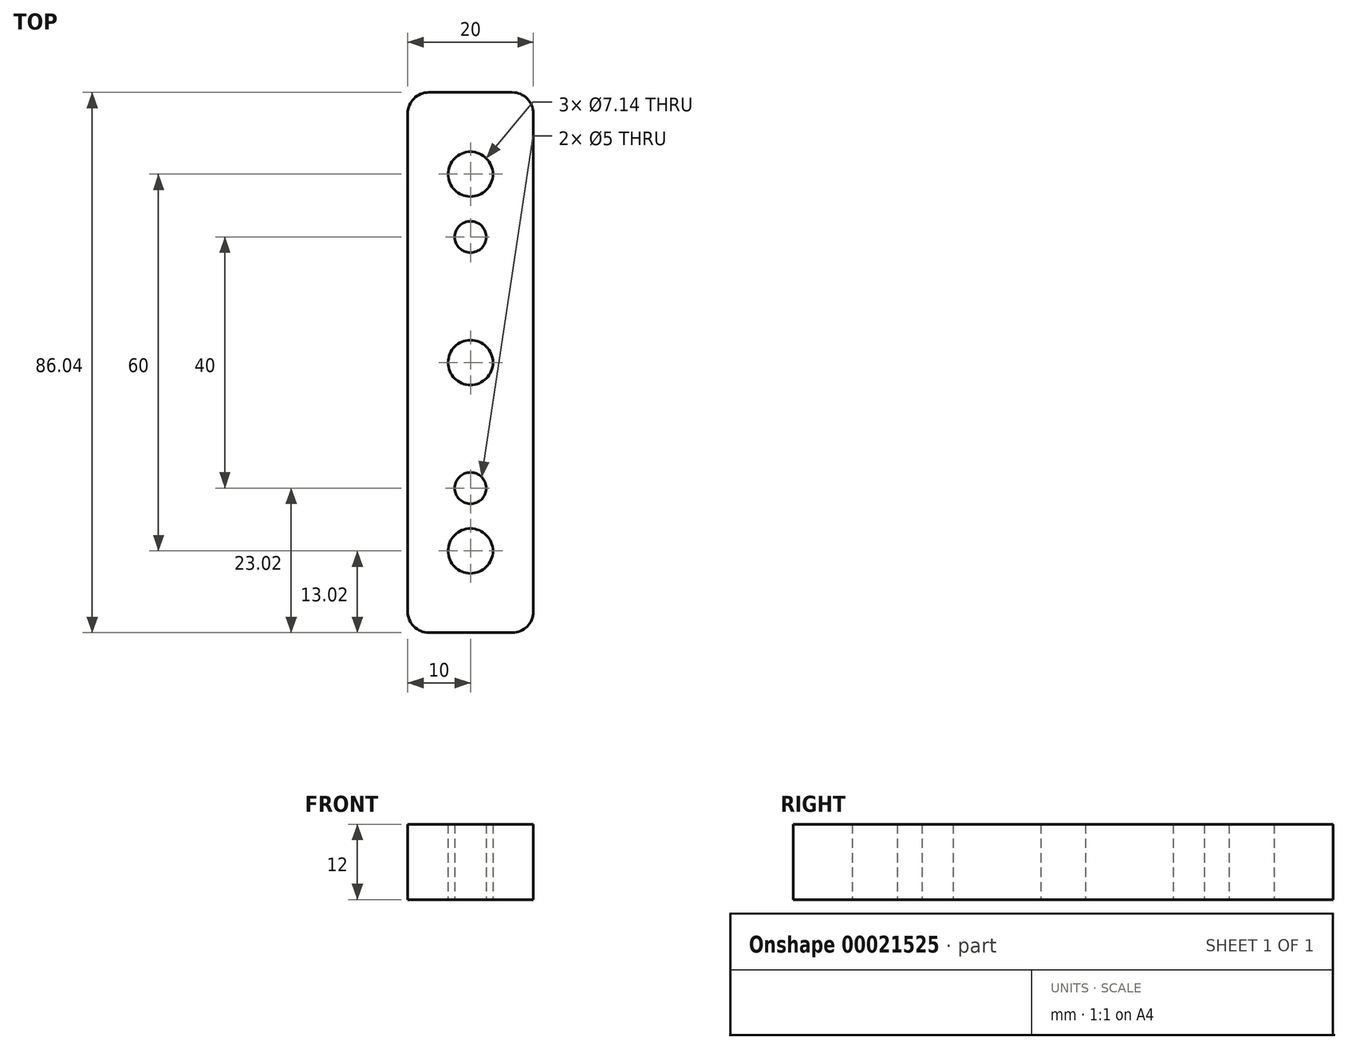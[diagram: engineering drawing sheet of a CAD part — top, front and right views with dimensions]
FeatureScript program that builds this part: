
annotation { "Feature Type Name" : "Feature", "Feature Type Description" : "" }
export const myFeature = defineFeature(function(context is Context, id is Id, definition is map)
    precondition{}
    {
        {
            var Q0;
            Q0=qCreatedBy(makeId("Top.planeOp"),FACE);
            var sketch = newSketch(context, id + "F0", { "sketchPlane" : qUnion([Q0])});
            skLineSegment(sketch, "E0.rect.bottom", {"start": v(6.64, -43.02) * mm, "end": v(-6.64, -43.02) * mm});
            skLineSegment(sketch, "E0.rect.top", {"start": v(6.64, 43.02) * mm, "end": v(-6.64, 43.02) * mm});
            skLineSegment(sketch, "E0.rect.left", {"start": v(10, -39.66) * mm, "end": v(10, 39.66) * mm});
            skLineSegment(sketch, "E0.rect.right", {"start": v(-10, -39.66) * mm, "end": v(-10, 39.66) * mm});
            skPoint(sketch, "E0.rect.middle", {"position": v(0, 0) * mm});
            skCircle(sketch, "E1", {"center": v(0, 0) * mm, "radius": 3.57 * mm});
            skCircle(sketch, "E2", {"center": v(0, -30) * mm, "radius": 3.57 * mm});
            skCircle(sketch, "E3", {"center": v(0, 30) * mm, "radius": 3.57 * mm});
            skCircle(sketch, "E4", {"center": v(0, 20) * mm, "radius": 2.5 * mm});
            skCircle(sketch, "E5", {"center": v(0, -20) * mm, "radius": 2.5 * mm});
            skPoint(sketch, "E6.visualSharp", {"position": v(-10, 43.02) * mm});
            skArc(sketch, "E6.filletArc", {"start": v(-6.64, 43.02) * mm, "mid": v(-9.02, 42.04) * mm, "end": v(-10, 39.66) * mm});
            skPoint(sketch, "E7.visualSharp", {"position": v(10, 43.02) * mm});
            skArc(sketch, "E7.filletArc", {"start": v(10, 39.66) * mm, "mid": v(9.02, 42.04) * mm, "end": v(6.64, 43.02) * mm});
            skPoint(sketch, "E8.visualSharp", {"position": v(10, -43.02) * mm});
            skArc(sketch, "E8.filletArc", {"start": v(6.64, -43.02) * mm, "mid": v(9.02, -42.04) * mm, "end": v(10, -39.66) * mm});
            skPoint(sketch, "E9.visualSharp", {"position": v(-10, -43.02) * mm});
            skArc(sketch, "E9.filletArc", {"start": v(-10, -39.66) * mm, "mid": v(-9.02, -42.04) * mm, "end": v(-6.64, -43.02) * mm});
            skSolve(sketch);
        }
        {
            var Q0;
            Q0=makeQuery(id+"F0.imprint","IMPRINT",FACE,{"disambiguationData":[TD([[makeQuery(id+"F0.imprint","IMPRINT",EDGE,{"derivedFrom":sQuery(id+"F0.wireOp",EDGE,"E0.rect.bottom")}),-1.0]])]});
            extrude(context, id + "F1", {"entities" : qUnion([Q0]), "depth" : 12 * mm});
        }
    });
